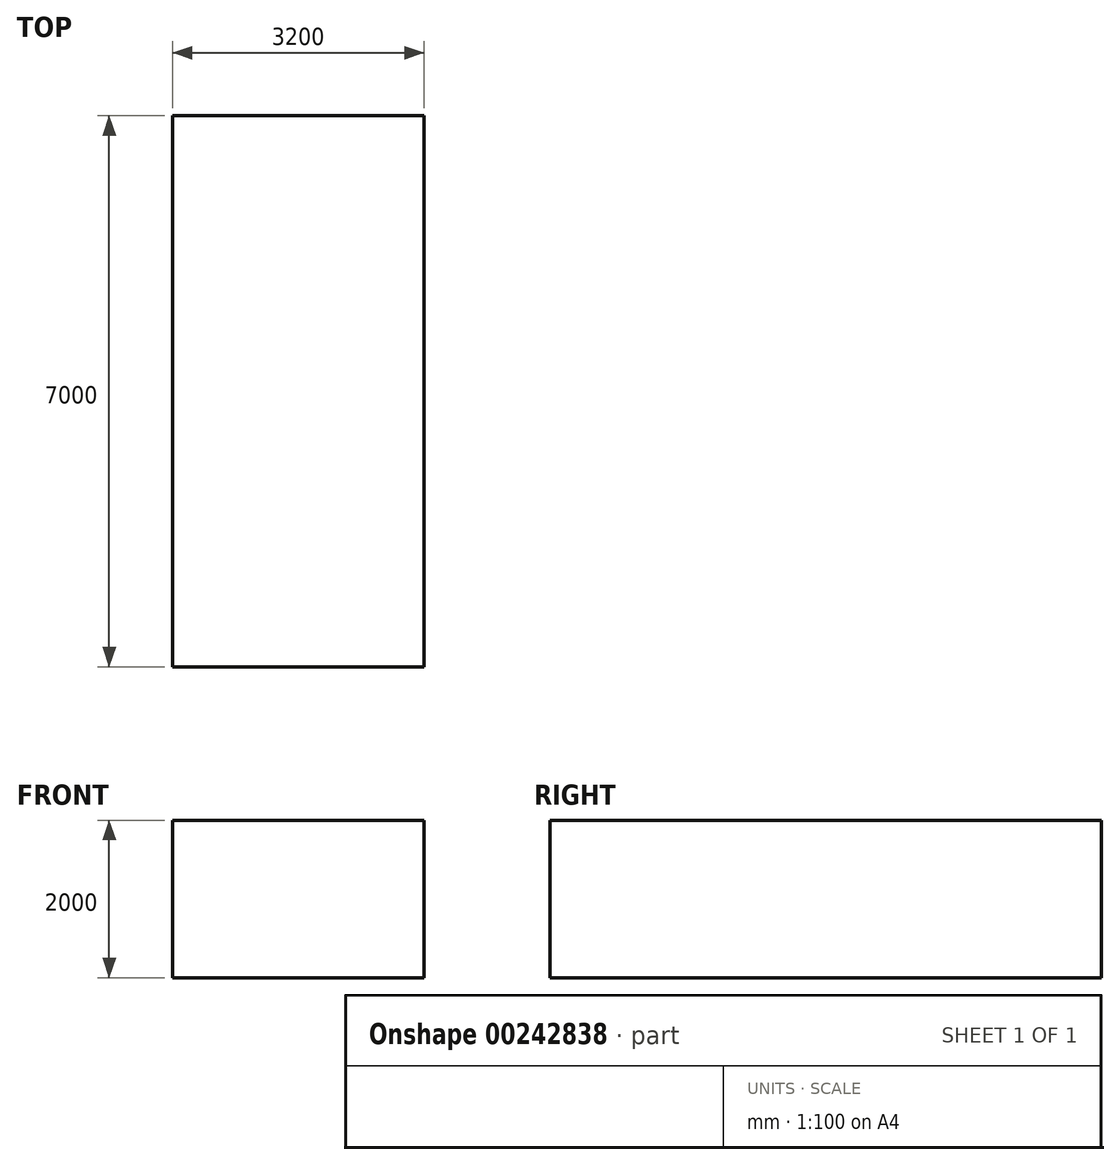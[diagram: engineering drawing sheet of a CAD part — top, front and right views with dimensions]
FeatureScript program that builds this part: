
annotation { "Feature Type Name" : "Feature", "Feature Type Description" : "" }
export const myFeature = defineFeature(function(context is Context, id is Id, definition is map)
    precondition{}
    {
        {
            var Q0;
            Q0=qCreatedBy(makeId("Right.planeOp"),FACE);
            var sketch = newSketch(context, id + "F0", { "sketchPlane" : qUnion([Q0])});
            skLineSegment(sketch, "E0.bottom", {"start": v(-3500, 1000) * mm, "end": v(3500, 1000) * mm});
            skLineSegment(sketch, "E0.top", {"start": v(-3500, -1000) * mm, "end": v(3500, -1000) * mm});
            skLineSegment(sketch, "E0.left", {"start": v(-3500, 1000) * mm, "end": v(-3500, -1000) * mm});
            skLineSegment(sketch, "E0.right", {"start": v(3500, 1000) * mm, "end": v(3500, -1000) * mm});
            skPoint(sketch, "E0.middle", {"position": v(0, 0) * mm});
            skSolve(sketch);
        }
        {
            var Q0;
            Q0=makeQuery(id+"F0.imprint","IMPRINT",FACE,{"disambiguationData":[TD([[makeQuery(id+"F0.imprint","IMPRINT",EDGE,{"derivedFrom":sQuery(id+"F0.wireOp",EDGE,"E0.bottom")}),-1.0]])]});
            extrude(context, id + "F1", {"entities" : qUnion([Q0]), "endBound" : BoundingType.SYMMETRIC, "depth" : 3200 * mm});
        }
    });
